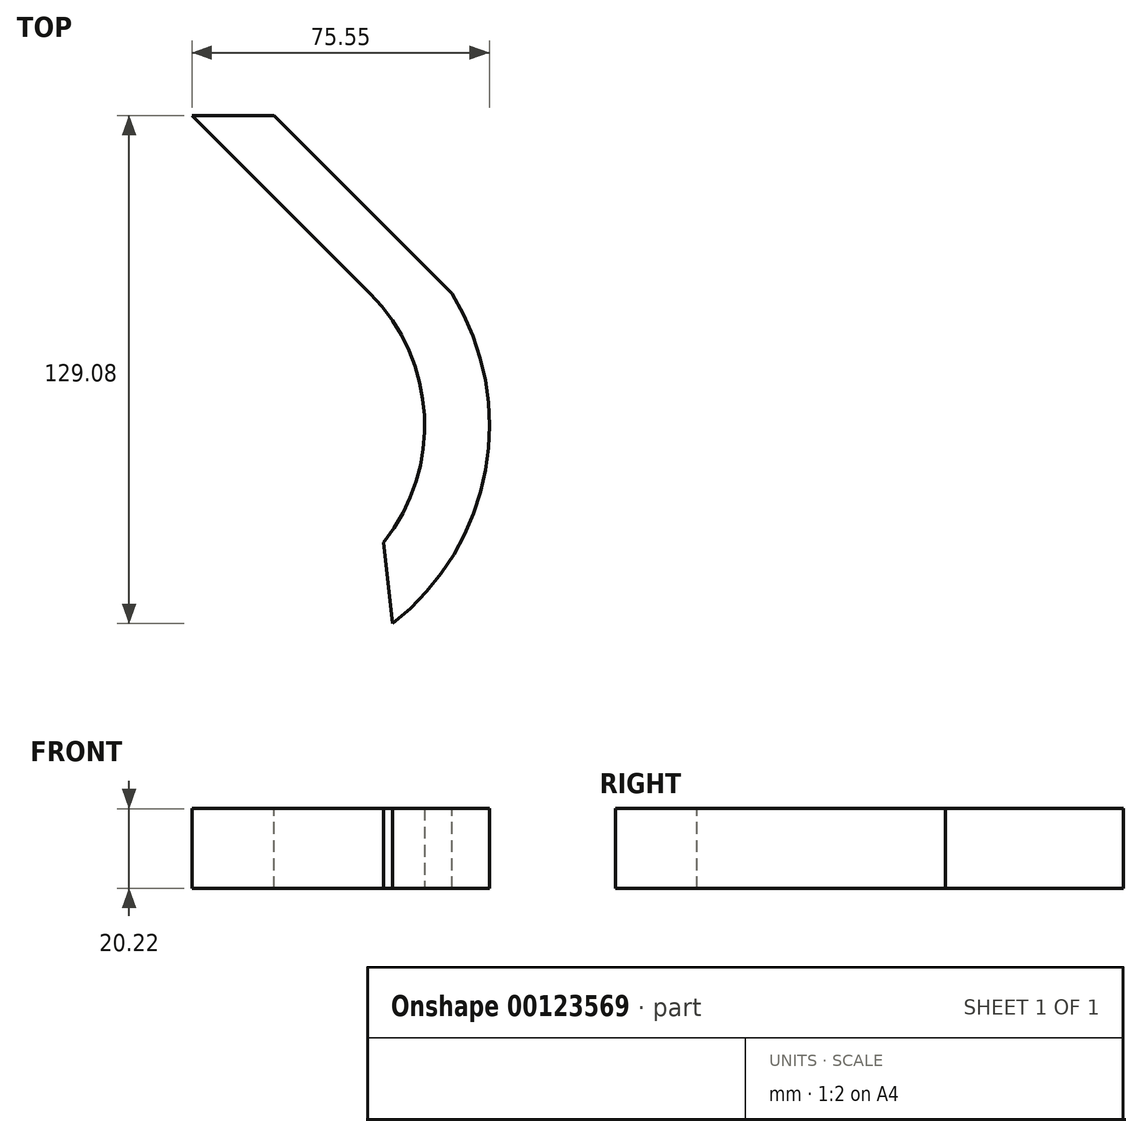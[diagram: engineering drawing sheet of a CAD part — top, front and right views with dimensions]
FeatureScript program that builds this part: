
annotation { "Feature Type Name" : "Feature", "Feature Type Description" : "" }
export const myFeature = defineFeature(function(context is Context, id is Id, definition is map)
    precondition{}
    {
        {
            var Q0;
            Q0=qCreatedBy(makeId("Front.planeOp"),FACE);
            var sketch = newSketch(context, id + "F0", { "sketchPlane" : qUnion([Q0])});
            skLineSegment(sketch, "E0.bottom", {"start": v(0, 0) * mm, "end": v(20.81, 0) * mm});
            skLineSegment(sketch, "E0.top", {"start": v(0, 20.22) * mm, "end": v(20.81, 20.22) * mm});
            skLineSegment(sketch, "E0.left", {"start": v(0, 0) * mm, "end": v(0, 20.22) * mm});
            skLineSegment(sketch, "E0.right", {"start": v(20.81, 0) * mm, "end": v(20.81, 20.22) * mm});
            skSolve(sketch);
        }
        {
            var Q0;
            Q0=qCreatedBy(makeId("Top.planeOp"),FACE);
            var sketch = newSketch(context, id + "F1", { "sketchPlane" : qUnion([Q0])});
            skLineSegment(sketch, "E1", {"start": v(0, 0) * mm, "end": v(45.25, -45.25) * mm});
            skArc(sketch, "E2", {"start": v(48.66, -108.4) * mm, "mid": v(59.04, -76.17) * mm, "end": v(45.25, -45.25) * mm});
            skSolve(sketch);
        }
        {
            var Q0;
            Q0=qCreatedBy(makeId("Top.planeOp"),FACE);
            var Q1;
            Q1=sQuery(id+"F0.wireOp",EDGE,"E0.top");
            cPlane(context, id + "F2", {"entities" : qUnion([Q0, Q1]), "cplaneType" : CPlaneType.LINE_ANGLE, "offset" : 25.4 * mm, "angle" : 0 * degree, "width" : 152.4 * mm, "height" : 152.4 * mm});
        }
        {
            var Q0;
            Q0=makeQuery(id+"F0.imprint","IMPRINT",FACE,{"disambiguationData":[TD([[makeQuery(id+"F0.imprint","IMPRINT",EDGE,{"derivedFrom":sQuery(id+"F0.wireOp",EDGE,"E0.bottom")}),1.0]])]});
            var Q1;
            Q1=sQuery(id+"F1.wireOp",EDGE,"E1");
            var Q2;
            Q2=sQuery(id+"F1.wireOp",EDGE,"E2");
            sweep(context, id + "F3", {"profiles" : qUnion([Q0]), "path" : qUnion([Q1, Q2])});
        }
    });
